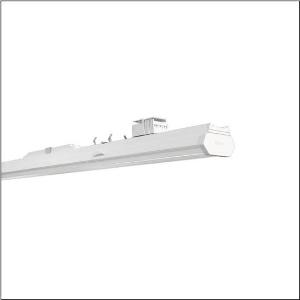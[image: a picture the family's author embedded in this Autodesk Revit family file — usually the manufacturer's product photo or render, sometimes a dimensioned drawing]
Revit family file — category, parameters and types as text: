
# Revit family: licross_11_protected_ho_51tp12mn4f5m
name_source: partatom
category: Lighting Fixtures
units: mm (PartAtom-declared; Revit-internal decimal feet)

## family parameters
Cut with Voids When Loaded = No
Host = Face
Light Source = No
Part Type = Normal
Room Calculation Point = No
Round Connector Dimension = Use Diameter
Shared = No

## types (1)
- --- (1 x LED, 15820 lm, 87.4 W, 4000K)
    Apparent Load = 87 VA
    CIE Flux Codes = 70 91 97 98 100
    Color Rendering = 80
    Color Temperature = 4000K
    Default Elevation = 1800 mm
    Description = Licross 11 Protected HO, luminaire insert, of sheet steel, galvanised, coil coated, white, length: 1.500mm, width: 90mm, height: 101mm, LED rated luminous flux: 15.820lm, light colour: 840, SDCM (Standard Deviation of Colour Matching)MacAdam ≤ 2 SDCM (initial), control gear: ON/OFF Multilumen, with plug, 3-pole, with phase selection, mains connection: 220..240V, AC, 50/60Hz, rated input power: 87W, internal wiring halogen-free, primary light control with lens, of plastic, primary optical cover: cover, of PMMA, light emission: direct distribution, primary light characteristic: symmetric, protection rating (complete): IP64, insulation class (complete): insulation class I (protective earthing), certification: CE, ENEC, VDE, UKCA, protection symbol: D if used in an environment with conductive dust loads with corresponding accessories, impact resistance: IK06, permissible ambient temperature for indoor applications: -35..+35°C, corresponds to IFS (International Featured Standards) requirements for safety and quality in the food industry, reducing of maximum allowable ambient temperature of 5°C with ceiling mounting, LABS conformity tested according to VDMA 24364:2018-05, The light source and the operating device comply with the requirements of the Ecodesign Regulation (EU) 2019/2020 and are replaceable in accordance with this regulation, packaging unit: 1 piece
    Height = 92 mm
    Lamp = 1 x LED
    Lamp Light Flux = 15820 lm
    Lamp Power = 87.4 W
    Lamp count = 1
    Length = 1500 mm
    Luminous efficacy = 181 lm/W
    Manufacturer = Siteco
    ModVariant = No
    Model = 51TP12MN4F5M
    Mounting Place = Ceiling
    Mounting Type = Pendant
    Number of Poles = 1
    OnlyDefault = Yes
    Power Factor = 1
    Product Name = Licross 11 Protected HO
    Product group = luminaire insert | ceiling pendant
    ProductGroupID = 901
    Protection Class = Protection class I
    Protection Degree = IP 64
    RLX_Detail_Level = 1
    RLX_Emergency_Light_Flux = 0 lm
    RLX_Emergency_Type = 0
    RLX_Emergency_Type_DB = No
    RlxData = <blob elided: 22333 chars, md5=0d473d9a>
    Socket = socket
    Standby Power = 0 W
    System Light Flux = 15820 lm
    System Power = 87 W
    Type Comments = factory setting: luminous flux: 100 % | (A | C | E) | 203 mA
    Type Image = l_1256148.jpg
    URL = http://relux.com
    VarID = @adj_092045
    Voltage = 0 V
    Weight = 0.00 kg
    Width = 88 mm

## geometry (parser evidence)
native form markers: Blend x4, Sweep x10
no freeform markers — native parametric forms only
